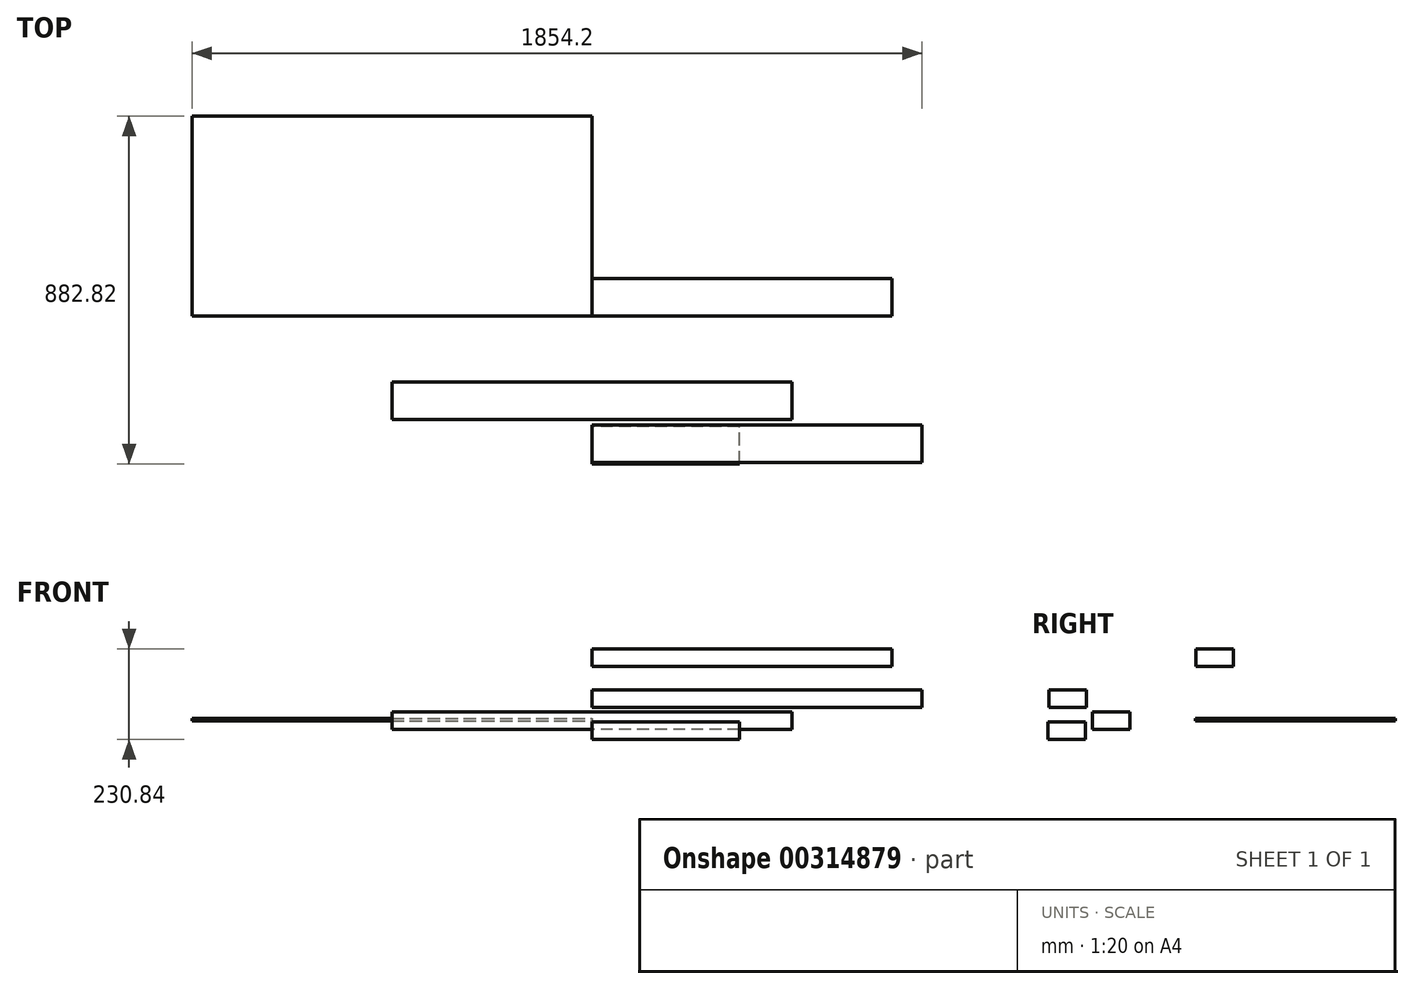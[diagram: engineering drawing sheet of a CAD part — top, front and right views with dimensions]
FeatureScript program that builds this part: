
annotation { "Feature Type Name" : "Feature", "Feature Type Description" : "" }
export const myFeature = defineFeature(function(context is Context, id is Id, definition is map)
    precondition{}
    {
        {
            var Q0;
            Q0=qCreatedBy(makeId("Right.planeOp"),FACE);
            var sketch = newSketch(context, id + "F0", { "sketchPlane" : qUnion([Q0])});
            skLineSegment(sketch, "E0.bottom", {"start": v(47.63, -22.22) * mm, "end": v(-47.63, -22.23) * mm});
            skLineSegment(sketch, "E0.top", {"start": v(47.63, 22.23) * mm, "end": v(-47.63, 22.22) * mm});
            skLineSegment(sketch, "E0.left", {"start": v(47.63, -22.22) * mm, "end": v(47.63, 22.23) * mm});
            skLineSegment(sketch, "E0.right", {"start": v(-47.63, -22.23) * mm, "end": v(-47.63, 22.22) * mm});
            skPoint(sketch, "E0.middle", {"position": v(0, 0) * mm});
            skSolve(sketch);
        }
        {
            var Q0;
            Q0=makeQuery(id+"F0.imprint","IMPRINT",FACE,{"disambiguationData":[TD([[makeQuery(id+"F0.imprint","IMPRINT",EDGE,{"derivedFrom":sQuery(id+"F0.wireOp",EDGE,"E0.bottom")}),-1.0]])]});
            extrude(context, id + "F1", {"entities" : qUnion([Q0]), "endBound" : BoundingType.SYMMETRIC, "depth" : 1016 * mm, "offsetDistance" : 25.4 * mm});
        }
        {
            var Q0;
            Q0=qCreatedBy(makeId("Right.planeOp"),FACE);
            var sketch = newSketch(context, id + "F2", { "sketchPlane" : qUnion([Q0])});
            skLineSegment(sketch, "E1.bottom", {"start": v(215.37, 138.52) * mm, "end": v(310.62, 138.52) * mm});
            skLineSegment(sketch, "E1.top", {"start": v(215.37, 182.97) * mm, "end": v(310.62, 182.97) * mm});
            skLineSegment(sketch, "E1.left", {"start": v(215.37, 138.52) * mm, "end": v(215.37, 182.97) * mm});
            skLineSegment(sketch, "E1.right", {"start": v(310.62, 138.52) * mm, "end": v(310.62, 182.97) * mm});
            skSolve(sketch);
        }
        {
            var Q0;
            Q0=makeQuery(id+"F2.imprint","IMPRINT",FACE,{"disambiguationData":[TD([[makeQuery(id+"F2.imprint","IMPRINT",EDGE,{"derivedFrom":sQuery(id+"F2.wireOp",EDGE,"E1.bottom")}),1.0]])]});
            extrude(context, id + "F3", {"entities" : qUnion([Q0]), "depth" : 762 * mm, "offsetDistance" : 25.4 * mm});
        }
        {
            var Q0;
            Q0=qCreatedBy(makeId("Right.planeOp"),FACE);
            var sketch = newSketch(context, id + "F4", { "sketchPlane" : qUnion([Q0])});
            skLineSegment(sketch, "E2.bottom", {"start": v(-157.4, 77.76) * mm, "end": v(-62.15, 77.76) * mm});
            skLineSegment(sketch, "E2.top", {"start": v(-157.4, 33.31) * mm, "end": v(-62.15, 33.31) * mm});
            skLineSegment(sketch, "E2.left", {"start": v(-157.4, 77.76) * mm, "end": v(-157.4, 33.31) * mm});
            skLineSegment(sketch, "E2.right", {"start": v(-62.15, 77.76) * mm, "end": v(-62.15, 33.31) * mm});
            skSolve(sketch);
        }
        {
            var Q0;
            Q0 = qSketchRegion(id + "F4", true);
            extrude(context, id + "F5", {"entities" : qUnion([Q0]), "depth" : 838.2 * mm, "offsetDistance" : 25.4 * mm});
        }
        {
            var Q0;
            Q0=qCreatedBy(makeId("Right.planeOp"),FACE);
            var sketch = newSketch(context, id + "F6", { "sketchPlane" : qUnion([Q0])});
            skLineSegment(sketch, "E3.bottom", {"start": v(-160.34, -3.42) * mm, "end": v(-65.1, -3.42) * mm});
            skLineSegment(sketch, "E3.top", {"start": v(-160.34, -47.87) * mm, "end": v(-65.1, -47.87) * mm});
            skLineSegment(sketch, "E3.left", {"start": v(-160.34, -3.42) * mm, "end": v(-160.34, -47.87) * mm});
            skLineSegment(sketch, "E3.right", {"start": v(-65.1, -3.42) * mm, "end": v(-65.1, -47.87) * mm});
            skSolve(sketch);
        }
        {
            var Q0;
            Q0 = qSketchRegion(id + "F6", true);
            extrude(context, id + "F7", {"entities" : qUnion([Q0]), "depth" : 374.65 * mm, "offsetDistance" : 25.4 * mm});
        }
        {
            var Q0;
            Q0=qCreatedBy(makeId("Top.planeOp"),FACE);
            var sketch = newSketch(context, id + "F8", { "sketchPlane" : qUnion([Q0])});
            skLineSegment(sketch, "E4.bottom", {"start": v(-1016, 722.48) * mm, "end": v(0, 722.48) * mm});
            skLineSegment(sketch, "E4.top", {"start": v(-1016, 214.48) * mm, "end": v(0, 214.48) * mm});
            skLineSegment(sketch, "E4.left", {"start": v(-1016, 722.48) * mm, "end": v(-1016, 214.48) * mm});
            skLineSegment(sketch, "E4.right", {"start": v(0, 722.48) * mm, "end": v(0, 214.48) * mm});
            skSolve(sketch);
        }
        {
            var Q0;
            Q0 = qSketchRegion(id + "F8", true);
            extrude(context, id + "F9", {"entities" : qUnion([Q0]), "depth" : 6.35 * mm, "offsetDistance" : 25.4 * mm});
        }
    });
